FCSTD DOCUMENT  (FreeCAD 1.2R45225 (Git))
Label: Assembly_LinkageUnit
License: All rights reserved
LicenseURL: https://en.wikipedia.org/wiki/All_rights_reserved
objects: App::Link×24, App::FeaturePython×8, App::Point×3, Assembly::AssemblyLink×2, Assembly::JointGroup×1, Assembly::AssemblyObject×1
EXTERNAL_REF file=RubberBandCollet.FCStd obj=Body
EXTERNAL_REF file=LinkageRod.FCStd obj=Body
EXTERNAL_REF file=Assembly_BallJointPlate.FCStd obj=Assembly
EXTERNAL_REF file=Assembly_BallJointPlate.FCStd obj=BallJointPlate
EXTERNAL_REF file=Assembly_BallJointPlate.FCStd obj=Ball
EXTERNAL_REF file=Assembly_BallJointPlate.FCStd obj=Ball001
EXTERNAL_REF file=Assembly_BallJointPlate.FCStd obj=RubberBand
EXTERNAL_REF file=Assembly_BallJointPlate.FCStd obj=RubberBand001
EXTERNAL_REF file=Assembly_BallJointPlate.FCStd obj=CrimpBead
EXTERNAL_REF file=Assembly_BallJointPlate.FCStd obj=CrimpBead001
EXTERNAL_REF file=Assembly_BallJointPlate.FCStd obj=CrimpBead002
EXTERNAL_REF file=Assembly_BallJointPlate.FCStd obj=CrimpBead003

FEATURE [App::Point] Origin001
  Role = Origin
FEATURE [App::Link] RubberBandCollet  label="RubberBandCollet2"
  LinkPlacement = pos=(8.5,24.5,4.02331e-07) rot=(0,0.707107,0.707107;3.14159rad)
  LinkedObject = -> <external RubberBandCollet.FCStd>#Body
  Placement = pos=(8.5,24.5,4.02331e-07) rot=(0,0.707107,0.707107;3.14159rad)
FEATURE [App::Link] RubberBandCollet001  label="RubberBandCollet1"
  LinkPlacement = pos=(-8.5,24.5,5.51344e-07) rot=(0,0.707107,0.707107;3.14159rad)
  LinkedObject = -> <external RubberBandCollet.FCStd>#Body
  Placement = pos=(-8.5,24.5,5.51344e-07) rot=(0,0.707107,0.707107;3.14159rad)
FEATURE [App::Link] RubberBandCollet002  label="RubberBandCollet3"
  LinkPlacement = pos=(-8.5,-24.5,-1.1921e-07) rot=(1,0,0;1.5708rad)
  LinkedObject = -> <external RubberBandCollet.FCStd>#Body
  Placement = pos=(-8.5,-24.5,-1.1921e-07) rot=(1,0,0;1.5708rad)
FEATURE [App::Link] RubberBandCollet003  label="RubberBandCollet4"
  LinkPlacement = pos=(8.5,-24.5,9.98377e-07) rot=(-1,0,0;1.5708rad)
  LinkedObject = -> <external RubberBandCollet.FCStd>#Body
  Placement = pos=(8.5,-24.5,9.98377e-07) rot=(-1,0,0;1.5708rad)
FEATURE [App::Link] LinkageRod  label="LinkageRod1"
  LinkPlacement = pos=(8.5,0,0) rot=(0,0,1;0rad)
  LinkedObject = -> <external LinkageRod.FCStd>#Body
  Placement = pos=(8.5,0,0) rot=(0,0,1;0rad)
FEATURE [App::Link] LinkageRod001  label="LinkageRod2"
  LinkPlacement = pos=(-8.5,0,0) rot=(0,0,1;0rad)
  LinkedObject = -> <external LinkageRod.FCStd>#Body
  Placement = pos=(-8.5,0,0) rot=(0,0,1;0rad)
FEATURE [App::Point] Origin003
  Role = Origin
FEATURE [App::Link] BallJointPlate002  label="BallJointPlate"
  LinkPlacement = pos=(0,0,-1.9) rot=(0,0,1;0rad)
  LinkedObject = -> <external Assembly_BallJointPlate.FCStd>#BallJointPlate
  Placement = pos=(0,0,-1.9) rot=(0,0,1;0rad)
FEATURE [App::Link] Ball004  label="Ball001"
  LinkPlacement = pos=(8.5,0,0) rot=(0,0,1;0rad)
  LinkedObject = -> <external Assembly_BallJointPlate.FCStd>#Ball
  Placement = pos=(8.5,0,0) rot=(0,0,1;0rad)
FEATURE [App::Link] Ball005  label="Ball002"
  LinkPlacement = pos=(-8.5,0,0) rot=(0,0,1;0rad)
  LinkedObject = -> <external Assembly_BallJointPlate.FCStd>#Ball001
  Placement = pos=(-8.5,0,0) rot=(0,0,1;0rad)
FEATURE [App::Link] RubberBand004  label="RubberBand001"
  LinkPlacement = pos=(8.5,0,13.35) rot=(-0.57735,0.57735,0.57735;4.18879rad)
  LinkedObject = -> <external Assembly_BallJointPlate.FCStd>#RubberBand
  Placement = pos=(8.5,0,13.35) rot=(-0.57735,0.57735,0.57735;4.18879rad)
FEATURE [App::Link] RubberBand005  label="RubberBand002"
  LinkPlacement = pos=(-8.5,0,13.35) rot=(0.57735,0.57735,0.57735;2.0944rad)
  LinkedObject = -> <external Assembly_BallJointPlate.FCStd>#RubberBand001
  Placement = pos=(-8.5,0,13.35) rot=(0.57735,0.57735,0.57735;2.0944rad)
FEATURE [App::Link] CrimpBead  label="CrimpBead1a"
  LinkPlacement = pos=(8.5,1.75,-2.4) rot=(0,0,1;1.5708rad)
  LinkedObject = -> <external Assembly_BallJointPlate.FCStd>#CrimpBead
  Placement = pos=(8.5,1.75,-2.4) rot=(0,0,1;1.5708rad)
FEATURE [App::Link] CrimpBead001  label="CrimpBead1b"
  LinkPlacement = pos=(8.5,-1.75,-2.4) rot=(0,0,1;1.5708rad)
  LinkedObject = -> <external Assembly_BallJointPlate.FCStd>#CrimpBead001
  Placement = pos=(8.5,-1.75,-2.4) rot=(0,0,1;1.5708rad)
FEATURE [App::Link] CrimpBead002  label="CrimpBead2a"
  LinkPlacement = pos=(-8.5,1.75,-2.4) rot=(0,0,-1;1.5708rad)
  LinkedObject = -> <external Assembly_BallJointPlate.FCStd>#CrimpBead002
  Placement = pos=(-8.5,1.75,-2.4) rot=(0,0,-1;1.5708rad)
FEATURE [App::Link] CrimpBead003  label="CrimpBead2b"
  LinkPlacement = pos=(-8.5,-1.75,-2.4) rot=(0,0,-1;1.5708rad)
  LinkedObject = -> <external Assembly_BallJointPlate.FCStd>#CrimpBead003
  Placement = pos=(-8.5,-1.75,-2.4) rot=(0,0,-1;1.5708rad)
FEATURE [Assembly::AssemblyLink] BallJointPlateAsm
  Group = -> [BallJointPlate002,Ball004,Ball005,RubberBand004,RubberBand005,CrimpBead,CrimpBead001,CrimpBead002,CrimpBead003]
  LinkedObject = -> <external Assembly_BallJointPlate.FCStd>#Assembly
  Origin = -> Origin002
  Placement = pos=(0,36.25,0) rot=(1,0,0;1.5708rad)
  Rigid = true
FEATURE [App::Point] Origin005  label="Origin006"
  Role = Origin
FEATURE [App::Link] BallJointPlate003  label="BallJointPlate001"
  LinkPlacement = pos=(0,0,-1.9) rot=(0,0,1;0rad)
  LinkedObject = -> <external Assembly_BallJointPlate.FCStd>#BallJointPlate
  Placement = pos=(0,0,-1.9) rot=(0,0,1;0rad)
FEATURE [App::Link] Ball006  label="Ball003"
  LinkPlacement = pos=(8.5,0,0) rot=(0,0,1;0rad)
  LinkedObject = -> <external Assembly_BallJointPlate.FCStd>#Ball
  Placement = pos=(8.5,0,0) rot=(0,0,1;0rad)
FEATURE [App::Link] Ball007  label="Ball004"
  LinkPlacement = pos=(-8.5,0,0) rot=(0,0,1;0rad)
  LinkedObject = -> <external Assembly_BallJointPlate.FCStd>#Ball001
  Placement = pos=(-8.5,0,0) rot=(0,0,1;0rad)
FEATURE [App::Link] RubberBand006  label="RubberBand003"
  LinkPlacement = pos=(8.5,0,13.35) rot=(-0.57735,0.57735,0.57735;4.18879rad)
  LinkedObject = -> <external Assembly_BallJointPlate.FCStd>#RubberBand
  Placement = pos=(8.5,0,13.35) rot=(-0.57735,0.57735,0.57735;4.18879rad)
FEATURE [App::Link] RubberBand007  label="RubberBand004"
  LinkPlacement = pos=(-8.5,0,13.35) rot=(0.57735,0.57735,0.57735;2.0944rad)
  LinkedObject = -> <external Assembly_BallJointPlate.FCStd>#RubberBand001
  Placement = pos=(-8.5,0,13.35) rot=(0.57735,0.57735,0.57735;2.0944rad)
FEATURE [App::Link] CrimpBead004  label="CrimpBead1a001"
  LinkPlacement = pos=(8.5,1.75,-2.4) rot=(0,0,1;1.5708rad)
  LinkedObject = -> <external Assembly_BallJointPlate.FCStd>#CrimpBead
  Placement = pos=(8.5,1.75,-2.4) rot=(0,0,1;1.5708rad)
FEATURE [App::Link] CrimpBead005  label="CrimpBead1b001"
  LinkPlacement = pos=(8.5,-1.75,-2.4) rot=(0,0,1;1.5708rad)
  LinkedObject = -> <external Assembly_BallJointPlate.FCStd>#CrimpBead001
  Placement = pos=(8.5,-1.75,-2.4) rot=(0,0,1;1.5708rad)
FEATURE [App::Link] CrimpBead006  label="CrimpBead2a001"
  LinkPlacement = pos=(-8.5,1.75,-2.4) rot=(0,0,-1;1.5708rad)
  LinkedObject = -> <external Assembly_BallJointPlate.FCStd>#CrimpBead002
  Placement = pos=(-8.5,1.75,-2.4) rot=(0,0,-1;1.5708rad)
FEATURE [App::Link] CrimpBead007  label="CrimpBead2b001"
  LinkPlacement = pos=(-8.5,-1.75,-2.4) rot=(0,0,-1;1.5708rad)
  LinkedObject = -> <external Assembly_BallJointPlate.FCStd>#CrimpBead003
  Placement = pos=(-8.5,-1.75,-2.4) rot=(0,0,-1;1.5708rad)
FEATURE [Assembly::AssemblyLink] BallJointPlateAsm001  label="BallJointPlateAsm"
  Group = -> [BallJointPlate003,Ball006,Ball007,RubberBand006,RubberBand007,CrimpBead004,CrimpBead005,CrimpBead006,CrimpBead007]
  LinkedObject = -> <external Assembly_BallJointPlate.FCStd>#Assembly
  Origin = -> Origin004
  Placement = pos=(0,-36.25,0) rot=(0,0.707107,0.707107;3.14159rad)
  Rigid = true
FEATURE [App::FeaturePython] GroundedJoint  label="GroundedJoint001"  # Assembly grounded joint (typed FeaturePython)
  ObjectToGround = -> BallJointPlateAsm
FEATURE [App::FeaturePython] GroundedJoint001  label="GroundedJoint002"  # Assembly grounded joint (typed FeaturePython)
  ObjectToGround = -> BallJointPlateAsm001
FEATURE [App::FeaturePython] GroundedJoint002  label="GroundedJoint003"  # Assembly grounded joint (typed FeaturePython)
  ObjectToGround = -> RubberBandCollet003
FEATURE [App::FeaturePython] GroundedJoint003  label="GroundedJoint004"  # Assembly grounded joint (typed FeaturePython)
  ObjectToGround = -> LinkageRod
FEATURE [App::FeaturePython] GroundedJoint004  label="GroundedJoint005"  # Assembly grounded joint (typed FeaturePython)
  ObjectToGround = -> LinkageRod001
FEATURE [App::FeaturePython] GroundedJoint005  label="GroundedJoint006"  # Assembly grounded joint (typed FeaturePython)
  ObjectToGround = -> RubberBandCollet001
FEATURE [App::FeaturePython] GroundedJoint006  label="GroundedJoint007"  # Assembly grounded joint (typed FeaturePython)
  ObjectToGround = -> RubberBandCollet
FEATURE [App::FeaturePython] GroundedJoint007  label="GroundedJoint008"  # Assembly grounded joint (typed FeaturePython)
  ObjectToGround = -> RubberBandCollet002
FEATURE [Assembly::JointGroup] Joints
  Group = -> [GroundedJoint,GroundedJoint001,GroundedJoint002,GroundedJoint003,GroundedJoint004,GroundedJoint005,GroundedJoint006,GroundedJoint007]
FEATURE [Assembly::AssemblyObject] Assembly  label="LinkageUnit"
  Group = -> [Joints,LinkageRod,LinkageRod001,RubberBandCollet001,RubberBandCollet,RubberBandCollet002,RubberBandCollet003,BallJointPlateAsm,BallJointPlateAsm001,GroundedJoint,GroundedJoint001,GroundedJoint002,GroundedJoint003,GroundedJoint004,GroundedJoint005,GroundedJoint006,GroundedJoint007]
  Origin = -> Origin
  Type = Assembly

RESOLVED EXTERNAL PARTS (link-assembly join: the EXTERNAL_REF files above that resolve inside this repo's crawl, each included once):
---- part Assembly_BallJointPlate.FCStd = doc fcstd_96c2e58f8617 ----
FCSTD DOCUMENT  (FreeCAD 1.2R45225 (Git))
Label: Assembly_BallJointPlate
License: All rights reserved
objects: App::Link×9, App::FeaturePython×9, App::Point×1, Assembly::JointGroup×1, Assembly::AssemblyObject×1
EXTERNAL_REF file=BallJointPlate.FCStd obj=Body
EXTERNAL_REF file=JointBall.FCStd obj=Body
EXTERNAL_REF file=RubberBand.FCStd obj=Body
EXTERNAL_REF file=CrimpBead.FCStd obj=Body

FEATURE [App::Point] Origin001
  Role = Origin
FEATURE [App::Link] BallJointPlate
  LinkPlacement = pos=(0,0,-1.9) rot=(0,0,1;0rad)
  LinkedObject = -> <external BallJointPlate.FCStd>#Body
  Placement = pos=(0,0,-1.9) rot=(0,0,1;0rad)
FEATURE [App::FeaturePython] GroundedJoint  # Assembly grounded joint (typed FeaturePython)
  ObjectToGround = -> BallJointPlate
FEATURE [App::Link] Ball  label="Ball1"
  LinkPlacement = pos=(8.5,0,0) rot=(0,0,1;0rad)
  LinkedObject = -> <external JointBall.FCStd>#Body
  Placement = pos=(8.5,0,0) rot=(0,0,1;0rad)
FEATURE [App::Link] Ball001  label="Ball2"
  LinkPlacement = pos=(-8.5,0,0) rot=(0,0,1;0rad)
  LinkedObject = -> <external JointBall.FCStd>#Body
  Placement = pos=(-8.5,0,0) rot=(0,0,1;0rad)
FEATURE [App::FeaturePython] Joint  label="ball1"  # Assembly joint (typed FeaturePython)
  Angle = 0
  AngleMax = 0
  AngleMin = 0
  Detach1 = false
  Detach2 = false
  Distance = 0
  Distance2 = 0
  EnableAngleMax = false
  EnableAngleMin = false
  EnableLengthMax = false
  EnableLengthMin = false
  JointType = 0 (Fixed)
  LengthMax = 0
  LengthMin = 0
  Offset1 = pos=(8.5,0,1.9) rot=(0,0,1;0rad)
  Placement1 = pos=(8.5,0,1.9) rot=(0,0,1;0rad)
  Reference1 = -> BallJointPlate
  Reference2 = -> Ball
  Suppressed = false
FEATURE [App::FeaturePython] Joint001  label="ball2"  # Assembly joint (typed FeaturePython)
  Angle = 0
  AngleMax = 0
  AngleMin = 0
  Detach1 = false
  Detach2 = false
  Distance = 0
  Distance2 = 0
  EnableAngleMax = false
  EnableAngleMin = false
  EnableLengthMax = false
  EnableLengthMin = false
  JointType = 0 (Fixed)
  LengthMax = 0
  LengthMin = 0
  Offset1 = pos=(-8.5,0,1.9) rot=(0,0,1;0rad)
  Placement1 = pos=(-8.5,0,1.9) rot=(0,0,1;0rad)
  Reference1 = -> BallJointPlate
  Reference2 = -> Ball001
  Suppressed = false
FEATURE [App::Link] RubberBand  label="RubberBand1"
  LinkPlacement = pos=(8.5,0,13.35) rot=(-0.57735,0.57735,0.57735;4.18879rad)
  LinkedObject = -> <external RubberBand.FCStd>#Body
  Placement = pos=(8.5,0,13.35) rot=(-0.57735,0.57735,0.57735;4.18879rad)
FEATURE [App::Link] RubberBand001  label="RubberBand2"
  LinkPlacement = pos=(-8.5,0,13.35) rot=(0.57735,0.57735,0.57735;2.0944rad)
  LinkedObject = -> <external RubberBand.FCStd>#Body
  Placement = pos=(-8.5,0,13.35) rot=(0.57735,0.57735,0.57735;2.0944rad)
FEATURE [App::FeaturePython] Joint002  label="rubber_band1"  # Assembly joint (typed FeaturePython)
  Angle = 0
  AngleMax = 0
  AngleMin = 0
  Detach1 = false
  Detach2 = false
  Distance = 0
  Distance2 = 0
  EnableAngleMax = false
  EnableAngleMin = false
  EnableLengthMax = false
  EnableLengthMin = false
  JointType = 0 (Fixed)
  LengthMax = 0
  LengthMin = 0
  Offset2 = pos=(8.5,0,15.25) rot=(0.57735,-0.57735,-0.57735;2.0944rad)
  Placement2 = pos=(8.5,0,15.25) rot=(0.57735,-0.57735,-0.57735;2.0944rad)
  Reference1 = -> RubberBand
  Reference2 = -> BallJointPlate
  Suppressed = false
FEATURE [App::FeaturePython] Joint003  label="rubber_band2"  # Assembly joint (typed FeaturePython)
  Angle = 0
  AngleMax = 0
  AngleMin = 0
  Detach1 = false
  Detach2 = false
  Distance = 0
  Distance2 = 0
  EnableAngleMax = false
  EnableAngleMin = false
  EnableLengthMax = false
  EnableLengthMin = false
  JointType = 0 (Fixed)
  LengthMax = 0
  LengthMin = 0
  Offset2 = pos=(-8.5,0,15.25) rot=(0.57735,0.57735,0.57735;2.0944rad)
  Placement2 = pos=(-8.5,0,15.25) rot=(0.57735,0.57735,0.57735;2.0944rad)
  Reference1 = -> RubberBand001
  Reference2 = -> BallJointPlate
  Suppressed = false
FEATURE [App::Link] CrimpBead  label="CrimpBead1a"
  LinkPlacement = pos=(8.5,1.75,-2.4) rot=(0,0,1;1.5708rad)
  LinkedObject = -> <external CrimpBead.FCStd>#Body
  Placement = pos=(8.5,1.75,-2.4) rot=(0,0,1;1.5708rad)
FEATURE [App::Link] CrimpBead001  label="CrimpBead1b"
  LinkPlacement = pos=(8.5,-1.75,-2.4) rot=(0,0,1;1.5708rad)
  LinkedObject = -> <external CrimpBead.FCStd>#Body
  Placement = pos=(8.5,-1.75,-2.4) rot=(0,0,1;1.5708rad)
FEATURE [App::FeaturePython] Joint004  label="crimp_bead1a"  # Assembly joint (typed FeaturePython)
  Angle = 0
  AngleMax = 0
  AngleMin = 0
  Detach1 = false
  Detach2 = false
  Distance = 0
  Distance2 = 0
  EnableAngleMax = false
  EnableAngleMin = false
  EnableLengthMax = false
  EnableLengthMin = false
  JointType = 0 (Fixed)
  LengthMax = 0
  LengthMin = 0
  Offset2 = pos=(8.5,1.75,-0.5) rot=(0,0,1;1.5708rad)
  Placement2 = pos=(8.5,1.75,-0.5) rot=(0,0,1;1.5708rad)
  Reference1 = -> CrimpBead
  Reference2 = -> BallJointPlate
  Suppressed = false
FEATURE [App::FeaturePython] Joint005  label="crimp_bead1b"  # Assembly joint (typed FeaturePython)
  Angle = 0
  AngleMax = 0
  AngleMin = 0
  Detach1 = false
  Detach2 = false
  Distance = 0
  Distance2 = 0
  EnableAngleMax = false
  EnableAngleMin = false
  EnableLengthMax = false
  EnableLengthMin = false
  JointType = 0 (Fixed)
  LengthMax = 0
  LengthMin = 0
  Offset2 = pos=(8.5,-1.75,-0.5) rot=(0,0,1;1.5708rad)
  Placement2 = pos=(8.5,-1.75,-0.5) rot=(0,0,1;1.5708rad)
  Reference1 = -> CrimpBead001
  Reference2 = -> BallJointPlate
  Suppressed = false
FEATURE [App::Link] CrimpBead002  label="CrimpBead2a"
  LinkPlacement = pos=(-8.5,1.75,-2.4) rot=(0,0,-1;1.5708rad)
  LinkedObject = -> <external CrimpBead.FCStd>#Body
  Placement = pos=(-8.5,1.75,-2.4) rot=(0,0,-1;1.5708rad)
FEATURE [App::Link] CrimpBead003  label="CrimpBead2b"
  LinkPlacement = pos=(-8.5,-1.75,-2.4) rot=(0,0,-1;1.5708rad)
  LinkedObject = -> <external CrimpBead.FCStd>#Body
  Placement = pos=(-8.5,-1.75,-2.4) rot=(0,0,-1;1.5708rad)
FEATURE [App::FeaturePython] Joint006  label="crimp_bead2b"  # Assembly joint (typed FeaturePython)
  Angle = 0
  AngleMax = 0
  AngleMin = 0
  Detach1 = false
  Detach2 = false
  Distance = 0
  Distance2 = 0
  EnableAngleMax = false
  EnableAngleMin = false
  EnableLengthMax = false
  EnableLengthMin = false
  JointType = 0 (Fixed)
  LengthMax = 0
  LengthMin = 0
  Offset2 = pos=(-8.5,-1.75,-0.5) rot=(0,0,-1;1.5708rad)
  Placement2 = pos=(-8.5,-1.75,-0.5) rot=(0,0,-1;1.5708rad)
  Reference1 = -> CrimpBead003
  Reference2 = -> BallJointPlate
  Suppressed = false
FEATURE [App::FeaturePython] Joint007  label="Fixed009"  # Assembly joint (typed FeaturePython)
  Angle = 0
  AngleMax = 0
  AngleMin = 0
  Detach1 = false
  Detach2 = false
  Distance = 0
  Distance2 = 0
  EnableAngleMax = false
  EnableAngleMin = false
  EnableLengthMax = false
  EnableLengthMin = false
  JointType = 0 (Fixed)
  LengthMax = 0
  LengthMin = 0
  Offset2 = pos=(-8.5,1.75,-0.5) rot=(0,0,-1;1.5708rad)
  Placement2 = pos=(-8.5,1.75,-0.5) rot=(0,0,-1;1.5708rad)
  Reference1 = -> CrimpBead002
  Reference2 = -> BallJointPlate
  Suppressed = false
FEATURE [Assembly::JointGroup] Joints
  Group = -> [GroundedJoint,Joint,Joint001,Joint002,Joint003,Joint004,Joint005,Joint006,Joint007]
FEATURE [Assembly::AssemblyObject] Assembly  label="BallJointPlateAsm"
  Group = -> [Joints,BallJointPlate,GroundedJoint,Ball,Ball001,Joint,Joint001,RubberBand,RubberBand001,Joint002,Joint003,CrimpBead,CrimpBead001,Joint004,Joint005,CrimpBead002,CrimpBead003,Joint006,Joint007]
  Origin = -> Origin
  Type = Assembly
---- part LinkageRod.FCStd = doc fcstd_1c6215430d7d ----
FCSTD DOCUMENT  (FreeCAD 1.2R45145 (Git))
Label: LinkageRod
License: All rights reserved
LicenseURL: https://en.wikipedia.org/wiki/All_rights_reserved
objects: Sketcher::SketchObject×2, App::Point×1, PartDesign::Pad×1, PartDesign::Chamfer×1, PartDesign::Groove×1, PartDesign::Mirrored×1, PartDesign::Body×1
note: 16 computed .brp shape members not serialized (recipe doc carries the construction recipe); baked Part::Feature solids carry a one-line shape summary decoded from their .brp

FEATURE [App::Point] Origin001
  Role = Origin
FEATURE [Sketcher::SketchObject] Sketch
  ArcFitTolerance = 1e-06
  AttachmentSupport = -> [XZ_Plane]
  ExternalTypes = [0]
  FullyConstrained = true
  MakeInternals = false
  MapMode = 5
  Placement = pos=(0,0,0) rot=(1,0,0;1.5708rad)
  sketch-geometry (1):
    g0: Circle CenterX=0 CenterY=0 CenterZ=0 NormalX=0 NormalY=0 NormalZ=1 AngleXU=0 Radius=1
  constraints (2):
    c: Coincident(g0,g-1)
    c: Diameter(g0) = 2
FEATURE [PartDesign::Pad] Pad
  Direction = (0,-1,2e-16)
  Length = 72
  Length2 = 10
  Placement = pos=(0,0,0) rot=(1,0,0;1.5708rad)
  Profile = -> Sketch
  ReferenceAxis = -> Sketch [N_Axis]
  Refine = true
  SideType = 2
  Suppressed = false
  Type = 0
  Type2 = 0
FEATURE [PartDesign::Chamfer] Chamfer
  Angle = 45
  Base = -> Pad [Edge3,Edge2]
  BaseFeature = -> Pad
  ChamferType = 1
  FlipDirection = false
  Placement = pos=(0,0,0) rot=(1,0,0;1.5708rad)
  Refine = true
  Size = 1
  Size2 = 0.4
  SupportTransform = false
  Suppressed = false
  UseAllEdges = false
FEATURE [Sketcher::SketchObject] Sketch002
  ArcFitTolerance = 1e-06
  AttachmentSupport = -> [Origin]
  ExternalTypes = [0]
  FullyConstrained = true
  MakeInternals = false
  MapMode = 5
  Placement = pos=(0,0,0) rot=(0.57735,0.57735,0.57735;2.0944rad)
  sketch-geometry (2):
    g0: ArcOfCircle CenterX=-36.25 CenterY=0 CenterZ=0 NormalX=0 NormalY=0 NormalZ=1 AngleXU=0 Radius=0.5 StartAngle=0 EndAngle=3.14159
    g1: LineSegment StartX=-36.75 StartY=1e-16 StartZ=0 EndX=-35.75 EndY=1e-16 EndZ=0
  constraints (7):
    c: PointOnObject(g0,g-1)
    c: DistanceX(g0,g-1) = 36.25
    c: Horizontal(g1)
    c: PointOnObject(g1,g-1)
    c: Diameter(g0) = 1
    c: Coincident(g1,g0)
    c: Coincident(g1,g0)
FEATURE [PartDesign::Groove] Groove
  Angle = 360
  Angle2 = 60
  Axis = (1e-16,1,-1e-16)
  Base = (0,0,0)
  BaseFeature = -> Chamfer
  Placement = pos=(0,0,0) rot=(1,0,0;1.5708rad)
  Profile = -> Sketch002
  ReferenceAxis = -> Y_Axis
  Refine = true
  Reversed = true
  Suppressed = false
  Type = 0
FEATURE [PartDesign::Mirrored] Mirrored
  BaseFeature = -> Groove
  MirrorPlane = -> XZ_Plane
  Originals = -> [Groove]
  Placement = pos=(0,0,0) rot=(1,0,0;1.5708rad)
  Refine = true
  Suppressed = false
  TransformMode = 0
FEATURE [PartDesign::Body] Body  label="LinkageRod"
  AllowCompound = false
  Group = -> [Sketch,Pad,Chamfer,Sketch002,Groove,Mirrored]
  Origin = -> Origin
  Tip = -> Mirrored
---- part RubberBandCollet.FCStd = doc fcstd_68d14b3e833f ----
FCSTD DOCUMENT  (FreeCAD 1.2R45145 (Git))
Label: RubberBandCollet
License: All rights reserved
LicenseURL: https://en.wikipedia.org/wiki/All_rights_reserved
objects: Sketcher::SketchObject×2, App::Point×1, PartDesign::Pad×1, PartDesign::Pocket×1, PartDesign::PolarPattern×1, PartDesign::Chamfer×1, PartDesign::Body×1
note: 16 computed .brp shape members not serialized (recipe doc carries the construction recipe); baked Part::Feature solids carry a one-line shape summary decoded from their .brp

FEATURE [App::Point] Origin001
  Role = Origin
FEATURE [Sketcher::SketchObject] Sketch
  ArcFitTolerance = 1e-06
  AttachmentSupport = -> [Origin]
  ExternalTypes = [0]
  FullyConstrained = true
  MakeInternals = false
  MapMode = 5
  sketch-geometry (8):
    g0: Circle CenterX=0 CenterY=0 CenterZ=0 NormalX=0 NormalY=0 NormalZ=1 AngleXU=0 Radius=1
    g1: ArcOfCircle CenterX=0 CenterY=1 CenterZ=0 NormalX=0 NormalY=0 NormalZ=1 AngleXU=0 Radius=2 StartAngle=2e-16 EndAngle=3.14159
    g2: ArcOfCircle CenterX=0 CenterY=-1 CenterZ=0 NormalX=0 NormalY=0 NormalZ=1 AngleXU=0 Radius=2 StartAngle=3.14159 EndAngle=6.28319
    g3: LineSegment StartX=2 StartY=1 StartZ=0 EndX=2 EndY=-1 EndZ=0
    g4: LineSegment StartX=-2 StartY=1 StartZ=0 EndX=-2 EndY=-1 EndZ=0
    g5: LineSegment [constr] StartX=0 StartY=1 StartZ=0 EndX=0 EndY=-1 EndZ=0
    g6: GeomPoint [constr] X=0 Y=-3 Z=0
    g7: GeomPoint [constr] X=0 Y=3 Z=0
  constraints (17):
    c: Coincident(g0,g-1)
    c: Diameter(g0) = 2
    c: Tangent(g1,g3) = 1.5708
    c: Tangent(g1,g4) = -1.5708
    c: Tangent(g2,g3) = 1.5708
    c: Tangent(g2,g4) = -1.5708
    c: Equal(g1,g2)
    c: Vertical(g4)
    c: Coincident(g5,g1)
    c: Coincident(g5,g2)
    c: Symmetric(g5,g5,g0)
    c: Distance(g3,g4) = 4
    c: PointOnObject(g6,g2)
    c: PointOnObject(g6,g-2)
    c: PointOnObject(g7,g1)
    c: PointOnObject(g7,g-2)
    c: DistanceY(g6,g7) = 6
FEATURE [PartDesign::Pad] Pad
  Direction = (0,0,1)
  Length = 3
  Length2 = 10
  Profile = -> Sketch
  ReferenceAxis = -> Sketch [N_Axis]
  Refine = true
  SideType = 2
  Suppressed = false
  Type = 0
  Type2 = 0
FEATURE [Sketcher::SketchObject] Sketch001
  ArcFitTolerance = 1e-06
  AttachmentSupport = -> [Pad]
  ExternalTypes = [0]
  FullyConstrained = true
  MakeInternals = false
  MapMode = 5
  Placement = pos=(0,0,1.5) rot=(0,0,1;0rad)
  sketch-geometry (5):
    g0: ArcOfCircle CenterX=0 CenterY=2 CenterZ=0 NormalX=0 NormalY=0 NormalZ=1 AngleXU=0 Radius=0.5 StartAngle=2.41886 EndAngle=7.00592
    g1: GeomPoint [constr] X=0 Y=3 Z=0
    g2: LineSegment StartX=-0.375 StartY=2.33072 StartZ=0 EndX=-0.375 EndY=4.33072 EndZ=0
    g3: LineSegment StartX=-0.375 StartY=4.33072 StartZ=0 EndX=0.375 EndY=4.33072 EndZ=0
    g4: LineSegment StartX=0.375 StartY=4.33072 StartZ=0 EndX=0.375 EndY=2.33072 EndZ=0
  constraints (15):
    c: PointOnObject(g0,g-2)
    c: PointOnObject(g1,g-3)
    c: PointOnObject(g1,g-2)
    c: Vertical(g2)
    c: Horizontal(g3)
    c: Vertical(g4)
    c: Horizontal(g4,g2)
    c: Coincident(g2,g3)
    c: Coincident(g3,g4)
    c: DistanceX(g3,g3) = 0.75
    c: Diameter(g0) = 1
    c: Coincident(g2,g0)
    c: Coincident(g4,g0)
    c: DistanceY(g4,g4) = 2
    c: DistanceY(g-1,g0) = 2
FEATURE [PartDesign::Pocket] Pocket
  BaseFeature = -> Pad
  Direction = (0,0,-1)
  Length = 5
  Length2 = 5
  Profile = -> Sketch001
  ReferenceAxis = -> Sketch001 [N_Axis]
  Refine = true
  SideType = 0
  Suppressed = false
  Type = 1
  Type2 = 0
FEATURE [PartDesign::PolarPattern] PolarPattern
  Angle = 360
  Axis = -> Z_Axis
  BaseFeature = -> Pocket
  Mode = 0
  Occurrences = 2
  Offset = 120
  Originals = -> [Pocket]
  Refine = true
  SpacingPattern = [0]
  Spacings = [-1]
  Suppressed = false
  TransformMode = 0
FEATURE [PartDesign::Chamfer] Chamfer
  Angle = 45
  Base = -> PolarPattern [Edge11,Edge25,Edge5,Edge19]
  BaseFeature = -> PolarPattern
  ChamferType = 0
  FlipDirection = false
  Refine = true
  Size = 0.4
  Size2 = 1
  SupportTransform = false
  Suppressed = false
  UseAllEdges = false
FEATURE [PartDesign::Body] Body  label="RubberBandCollet"
  AllowCompound = false
  Group = -> [Sketch,Pad,Sketch001,Pocket,PolarPattern,Chamfer]
  Origin = -> Origin
  Tip = -> Chamfer
